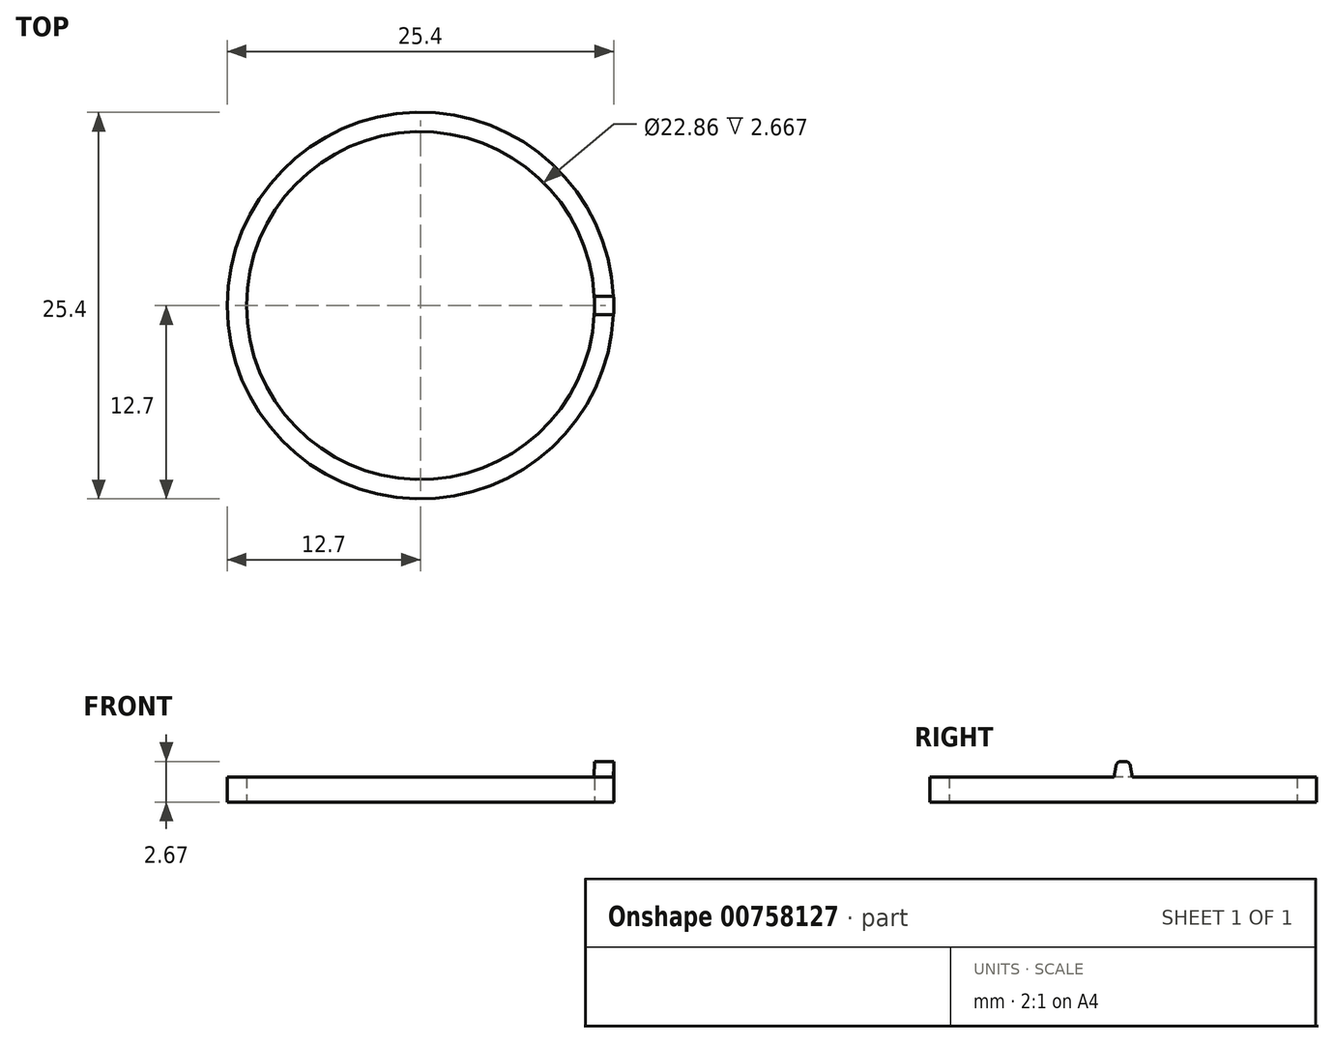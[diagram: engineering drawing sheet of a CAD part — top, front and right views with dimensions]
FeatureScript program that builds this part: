
annotation { "Feature Type Name" : "Feature", "Feature Type Description" : "" }
export const myFeature = defineFeature(function(context is Context, id is Id, definition is map)
    precondition{}
    {
        {
            var Q0;
            Q0=qCreatedBy(makeId("Top.planeOp"),FACE);
            var sketch = newSketch(context, id + "F0", { "sketchPlane" : qUnion([Q0])});
            skCircle(sketch, "E0", {"center": v(0, 0) * mm, "radius": 9.52 * mm});
            skCircle(sketch, "E1", {"center": v(0, 0) * mm, "radius": 12.7 * mm});
            skSolve(sketch);
        }
        {
            var Q0;
            Q0 = qSketchRegion(id + "F0", true);
            extrude(context, id + "F1", {"entities" : qUnion([Q0]), "depth" : 9.27 * mm, "offsetDistance" : 25.4 * mm});
        }
        {
            var Q0;
            Q0=makeQuery(id+"F1.opExtrude","CAP_FACE",FACE,{"disambiguationData":[OSD([sQuery(id+"F0.wireOp",EDGE,"E0"),sQuery(id+"F0.wireOp",EDGE,"E1")])],"isStart":false});
            var sketch = newSketch(context, id + "F2", { "sketchPlane" : qUnion([Q0])});
            skCircle(sketch, "E2", {"center": v(0, 0) * mm, "radius": 19.05 * mm});
            skCircle(sketch, "E3", {"center": v(0, 0) * mm, "radius": 10.8 * mm});
            skSolve(sketch);
        }
        {
            var Q0;
            Q0=makeQuery(id+"F2.imprint","IMPRINT",FACE,{"disambiguationData":[TD([[makeQuery(id+"F2.imprint","IMPRINT",EDGE,{"derivedFrom":sQuery(id+"F2.wireOp",EDGE,"E3")}),-1.0]])]});
            extrude(context, id + "F3", {"entities" : qUnion([Q0]), "operationType" : NewBodyOperationType.REMOVE, "oppositeDirection" : true, "depth" : 7.62 * mm, "offsetDistance" : 25.4 * mm});
        }
        {
            var Q0;
            Q0=qCreatedBy(makeId("Right.planeOp"),FACE);
            cPlane(context, id + "F4", {"entities" : qUnion([Q0]), "cplaneType" : CPlaneType.OFFSET, "offset" : 10.16 * mm, "width" : 152.4 * mm, "height" : 152.4 * mm});
        }
        {
            var Q0;
            Q0=qCreatedBy(id+"F4.planeOp",FACE);
            var sketch = newSketch(context, id + "F5", { "sketchPlane" : qUnion([Q0])});
            skLineSegment(sketch, "E4", {"start": v(-0.6, 1.65) * mm, "end": v(-0.42, 2.67) * mm});
            skLineSegment(sketch, "E5", {"start": v(-0.42, 2.67) * mm, "end": v(0.42, 2.67) * mm});
            skLineSegment(sketch, "E6", {"start": v(0.42, 2.67) * mm, "end": v(0.6, 1.65) * mm});
            skLineSegment(sketch, "E7", {"start": v(-0.6, 1.65) * mm, "end": v(0.6, 1.65) * mm});
            skSolve(sketch);
        }
        {
            var Q0;
            Q0 = qSketchRegion(id + "F5", true);
            var Q1;
            Q1=makeQuery(id+"F1.opExtrude","SWEPT_FACE",FACE,{"disambiguationData":[OSD([sQuery(id+"F0.wireOp",EDGE,"E1")])]});
            extrude(context, id + "F6", {"entities" : qUnion([Q0]), "operationType" : NewBodyOperationType.ADD, "endBound" : BoundingType.UP_TO_SURFACE, "depth" : 25.4 * mm, "endBoundEntityFace" : qUnion([Q1]), "offsetDistance" : 25.4 * mm});
        }
        {
            var Q0;
            Q0=qCreatedBy(makeId("Front.planeOp"),FACE);
            var sketch = newSketch(context, id + "F7", { "sketchPlane" : qUnion([Q0])});
            skLineSegment(sketch, "E8", {"start": v(0, 28.15) * mm, "end": v(0, -16.82) * mm});
            skSolve(sketch);
        }
        {
            var Q0;
            Q0=makeQuery(id+"FndBxbkuIEqvg3Y_1.3.F6.opExtrude","SWEPT_EDGE",EDGE,{"disambiguationData":[OSD([sQuery(id+"F5.wireOp",EDGE,"E6"),sQuery(id+"F5.wireOp",EDGE,"E7")])]});
            var Q1;
            Q1=makeQuery(id+"FndBxbkuIEqvg3Y_1.3.F6.opExtrude","SWEPT_EDGE",EDGE,{"disambiguationData":[OSD([sQuery(id+"F5.wireOp",EDGE,"E5"),sQuery(id+"F5.wireOp",EDGE,"E6")])]});
            var Q2;
            Q2=makeQuery(id+"FndBxbkuIEqvg3Y_1.3.F6.opExtrude","SWEPT_EDGE",EDGE,{"disambiguationData":[OSD([sQuery(id+"F5.wireOp",EDGE,"E4"),sQuery(id+"F5.wireOp",EDGE,"E5")])]});
            var Q3;
            Q3=makeQuery(id+"FndBxbkuIEqvg3Y_1.3.F6.opExtrude","SWEPT_EDGE",EDGE,{"disambiguationData":[OSD([sQuery(id+"F5.wireOp",EDGE,"E4"),sQuery(id+"F5.wireOp",EDGE,"E7")])]});
            var Q4;
            Q4=makeQuery(id+"FndBxbkuIEqvg3Y_1.2.F6.opExtrude","SWEPT_EDGE",EDGE,{"disambiguationData":[OSD([sQuery(id+"F5.wireOp",EDGE,"E4"),sQuery(id+"F5.wireOp",EDGE,"E7")])]});
            var Q5;
            Q5=makeQuery(id+"FndBxbkuIEqvg3Y_1.2.F6.opExtrude","SWEPT_EDGE",EDGE,{"disambiguationData":[OSD([sQuery(id+"F5.wireOp",EDGE,"E4"),sQuery(id+"F5.wireOp",EDGE,"E5")])]});
            var Q6;
            Q6=makeQuery(id+"FndBxbkuIEqvg3Y_1.2.F6.opExtrude","SWEPT_EDGE",EDGE,{"disambiguationData":[OSD([sQuery(id+"F5.wireOp",EDGE,"E5"),sQuery(id+"F5.wireOp",EDGE,"E6")])]});
            var Q7;
            Q7=makeQuery(id+"FndBxbkuIEqvg3Y_1.2.F6.opExtrude","SWEPT_EDGE",EDGE,{"disambiguationData":[OSD([sQuery(id+"F5.wireOp",EDGE,"E6"),sQuery(id+"F5.wireOp",EDGE,"E7")])]});
            var Q8;
            Q8=makeQuery(id+"FndBxbkuIEqvg3Y_1.1.F6.opExtrude","SWEPT_EDGE",EDGE,{"disambiguationData":[OSD([sQuery(id+"F5.wireOp",EDGE,"E4"),sQuery(id+"F5.wireOp",EDGE,"E7")])]});
            var Q9;
            Q9=makeQuery(id+"FndBxbkuIEqvg3Y_1.1.F6.opExtrude","SWEPT_EDGE",EDGE,{"disambiguationData":[OSD([sQuery(id+"F5.wireOp",EDGE,"E4"),sQuery(id+"F5.wireOp",EDGE,"E5")])]});
            var Q10;
            Q10=makeQuery(id+"FndBxbkuIEqvg3Y_1.1.F6.opExtrude","SWEPT_EDGE",EDGE,{"disambiguationData":[OSD([sQuery(id+"F5.wireOp",EDGE,"E5"),sQuery(id+"F5.wireOp",EDGE,"E6")])]});
            var Q11;
            Q11=makeQuery(id+"FndBxbkuIEqvg3Y_1.1.F6.opExtrude","SWEPT_EDGE",EDGE,{"disambiguationData":[OSD([sQuery(id+"F5.wireOp",EDGE,"E6"),sQuery(id+"F5.wireOp",EDGE,"E7")])]});
            var Q12;
            Q12=makeQuery(id+"F6.opExtrude","SWEPT_EDGE",EDGE,{"disambiguationData":[OSD([sQuery(id+"F5.wireOp",EDGE,"E4"),sQuery(id+"F5.wireOp",EDGE,"E7")])]});
            var Q13;
            Q13=makeQuery(id+"F6.opExtrude","SWEPT_EDGE",EDGE,{"disambiguationData":[OSD([sQuery(id+"F5.wireOp",EDGE,"E4"),sQuery(id+"F5.wireOp",EDGE,"E5")])]});
            var Q14;
            Q14=makeQuery(id+"F6.opExtrude","SWEPT_EDGE",EDGE,{"disambiguationData":[OSD([sQuery(id+"F5.wireOp",EDGE,"E5"),sQuery(id+"F5.wireOp",EDGE,"E6")])]});
            var Q15;
            Q15=makeQuery(id+"F6.opExtrude","SWEPT_EDGE",EDGE,{"disambiguationData":[OSD([sQuery(id+"F5.wireOp",EDGE,"E6"),sQuery(id+"F5.wireOp",EDGE,"E7")])]});
            var Q16;
            Q16=makeQuery(id+"FndBxbkuIEqvg3Y_1.31.F6.opExtrude","SWEPT_EDGE",EDGE,{"disambiguationData":[OSD([sQuery(id+"F5.wireOp",EDGE,"E4"),sQuery(id+"F5.wireOp",EDGE,"E7")])]});
            var Q17;
            Q17=makeQuery(id+"FndBxbkuIEqvg3Y_1.31.F6.opExtrude","SWEPT_EDGE",EDGE,{"disambiguationData":[OSD([sQuery(id+"F5.wireOp",EDGE,"E4"),sQuery(id+"F5.wireOp",EDGE,"E5")])]});
            var Q18;
            Q18=makeQuery(id+"FndBxbkuIEqvg3Y_1.31.F6.opExtrude","SWEPT_EDGE",EDGE,{"disambiguationData":[OSD([sQuery(id+"F5.wireOp",EDGE,"E5"),sQuery(id+"F5.wireOp",EDGE,"E6")])]});
            var Q19;
            Q19=makeQuery(id+"FndBxbkuIEqvg3Y_1.31.F6.opExtrude","SWEPT_EDGE",EDGE,{"disambiguationData":[OSD([sQuery(id+"F5.wireOp",EDGE,"E6"),sQuery(id+"F5.wireOp",EDGE,"E7")])]});
            var Q20;
            Q20=makeQuery(id+"FndBxbkuIEqvg3Y_1.30.F6.opExtrude","SWEPT_EDGE",EDGE,{"disambiguationData":[OSD([sQuery(id+"F5.wireOp",EDGE,"E4"),sQuery(id+"F5.wireOp",EDGE,"E7")])]});
            var Q21;
            Q21=makeQuery(id+"FndBxbkuIEqvg3Y_1.30.F6.opExtrude","SWEPT_EDGE",EDGE,{"disambiguationData":[OSD([sQuery(id+"F5.wireOp",EDGE,"E4"),sQuery(id+"F5.wireOp",EDGE,"E5")])]});
            var Q22;
            Q22=makeQuery(id+"FndBxbkuIEqvg3Y_1.30.F6.opExtrude","SWEPT_EDGE",EDGE,{"disambiguationData":[OSD([sQuery(id+"F5.wireOp",EDGE,"E5"),sQuery(id+"F5.wireOp",EDGE,"E6")])]});
            var Q23;
            Q23=makeQuery(id+"FndBxbkuIEqvg3Y_1.30.F6.opExtrude","SWEPT_EDGE",EDGE,{"disambiguationData":[OSD([sQuery(id+"F5.wireOp",EDGE,"E6"),sQuery(id+"F5.wireOp",EDGE,"E7")])]});
            var Q24;
            Q24=makeQuery(id+"FndBxbkuIEqvg3Y_1.29.F6.opExtrude","SWEPT_EDGE",EDGE,{"disambiguationData":[OSD([sQuery(id+"F5.wireOp",EDGE,"E4"),sQuery(id+"F5.wireOp",EDGE,"E7")])]});
            var Q25;
            Q25=makeQuery(id+"FndBxbkuIEqvg3Y_1.29.F6.opExtrude","SWEPT_EDGE",EDGE,{"disambiguationData":[OSD([sQuery(id+"F5.wireOp",EDGE,"E4"),sQuery(id+"F5.wireOp",EDGE,"E5")])]});
            var Q26;
            Q26=makeQuery(id+"FndBxbkuIEqvg3Y_1.29.F6.opExtrude","SWEPT_EDGE",EDGE,{"disambiguationData":[OSD([sQuery(id+"F5.wireOp",EDGE,"E5"),sQuery(id+"F5.wireOp",EDGE,"E6")])]});
            var Q27;
            Q27=makeQuery(id+"FndBxbkuIEqvg3Y_1.29.F6.opExtrude","SWEPT_EDGE",EDGE,{"disambiguationData":[OSD([sQuery(id+"F5.wireOp",EDGE,"E6"),sQuery(id+"F5.wireOp",EDGE,"E7")])]});
            var Q28;
            Q28=makeQuery(id+"FndBxbkuIEqvg3Y_1.28.F6.opExtrude","SWEPT_EDGE",EDGE,{"disambiguationData":[OSD([sQuery(id+"F5.wireOp",EDGE,"E4"),sQuery(id+"F5.wireOp",EDGE,"E5")])]});
            var Q29;
            Q29=makeQuery(id+"FndBxbkuIEqvg3Y_1.28.F6.opExtrude","SWEPT_EDGE",EDGE,{"disambiguationData":[OSD([sQuery(id+"F5.wireOp",EDGE,"E4"),sQuery(id+"F5.wireOp",EDGE,"E7")])]});
            var Q30;
            Q30=makeQuery(id+"FndBxbkuIEqvg3Y_1.28.F6.opExtrude","SWEPT_EDGE",EDGE,{"disambiguationData":[OSD([sQuery(id+"F5.wireOp",EDGE,"E5"),sQuery(id+"F5.wireOp",EDGE,"E6")])]});
            var Q31;
            Q31=makeQuery(id+"FndBxbkuIEqvg3Y_1.28.F6.opExtrude","SWEPT_EDGE",EDGE,{"disambiguationData":[OSD([sQuery(id+"F5.wireOp",EDGE,"E6"),sQuery(id+"F5.wireOp",EDGE,"E7")])]});
            var Q32;
            Q32=makeQuery(id+"FndBxbkuIEqvg3Y_1.27.F6.opExtrude","SWEPT_EDGE",EDGE,{"disambiguationData":[OSD([sQuery(id+"F5.wireOp",EDGE,"E4"),sQuery(id+"F5.wireOp",EDGE,"E7")])]});
            var Q33;
            Q33=makeQuery(id+"FndBxbkuIEqvg3Y_1.27.F6.opExtrude","SWEPT_EDGE",EDGE,{"disambiguationData":[OSD([sQuery(id+"F5.wireOp",EDGE,"E4"),sQuery(id+"F5.wireOp",EDGE,"E5")])]});
            var Q34;
            Q34=makeQuery(id+"FndBxbkuIEqvg3Y_1.27.F6.opExtrude","SWEPT_EDGE",EDGE,{"disambiguationData":[OSD([sQuery(id+"F5.wireOp",EDGE,"E5"),sQuery(id+"F5.wireOp",EDGE,"E6")])]});
            var Q35;
            Q35=makeQuery(id+"FndBxbkuIEqvg3Y_1.26.F6.opExtrude","SWEPT_EDGE",EDGE,{"disambiguationData":[OSD([sQuery(id+"F5.wireOp",EDGE,"E4"),sQuery(id+"F5.wireOp",EDGE,"E7")])]});
            var Q36;
            Q36=makeQuery(id+"FndBxbkuIEqvg3Y_1.26.F6.opExtrude","SWEPT_EDGE",EDGE,{"disambiguationData":[OSD([sQuery(id+"F5.wireOp",EDGE,"E4"),sQuery(id+"F5.wireOp",EDGE,"E5")])]});
            var Q37;
            Q37=makeQuery(id+"FndBxbkuIEqvg3Y_1.26.F6.opExtrude","SWEPT_EDGE",EDGE,{"disambiguationData":[OSD([sQuery(id+"F5.wireOp",EDGE,"E5"),sQuery(id+"F5.wireOp",EDGE,"E6")])]});
            var Q38;
            Q38=makeQuery(id+"FndBxbkuIEqvg3Y_1.25.F6.opExtrude","SWEPT_EDGE",EDGE,{"disambiguationData":[OSD([sQuery(id+"F5.wireOp",EDGE,"E4"),sQuery(id+"F5.wireOp",EDGE,"E7")])]});
            var Q39;
            Q39=makeQuery(id+"FndBxbkuIEqvg3Y_1.25.F6.opExtrude","SWEPT_EDGE",EDGE,{"disambiguationData":[OSD([sQuery(id+"F5.wireOp",EDGE,"E4"),sQuery(id+"F5.wireOp",EDGE,"E5")])]});
            var Q40;
            Q40=makeQuery(id+"FndBxbkuIEqvg3Y_1.25.F6.opExtrude","SWEPT_EDGE",EDGE,{"disambiguationData":[OSD([sQuery(id+"F5.wireOp",EDGE,"E5"),sQuery(id+"F5.wireOp",EDGE,"E6")])]});
            var Q41;
            Q41=makeQuery(id+"FndBxbkuIEqvg3Y_1.27.F6.opExtrude","SWEPT_EDGE",EDGE,{"disambiguationData":[OSD([sQuery(id+"F5.wireOp",EDGE,"E6"),sQuery(id+"F5.wireOp",EDGE,"E7")])]});
            var Q42;
            Q42=makeQuery(id+"FndBxbkuIEqvg3Y_1.26.F6.opExtrude","SWEPT_EDGE",EDGE,{"disambiguationData":[OSD([sQuery(id+"F5.wireOp",EDGE,"E6"),sQuery(id+"F5.wireOp",EDGE,"E7")])]});
            var Q43;
            Q43=makeQuery(id+"FndBxbkuIEqvg3Y_1.25.F6.opExtrude","SWEPT_EDGE",EDGE,{"disambiguationData":[OSD([sQuery(id+"F5.wireOp",EDGE,"E6"),sQuery(id+"F5.wireOp",EDGE,"E7")])]});
            var Q44;
            Q44=makeQuery(id+"FndBxbkuIEqvg3Y_1.4.F6.opExtrude","SWEPT_EDGE",EDGE,{"disambiguationData":[OSD([sQuery(id+"F5.wireOp",EDGE,"E6"),sQuery(id+"F5.wireOp",EDGE,"E7")])]});
            var Q45;
            Q45=makeQuery(id+"FndBxbkuIEqvg3Y_1.4.F6.opExtrude","SWEPT_EDGE",EDGE,{"disambiguationData":[OSD([sQuery(id+"F5.wireOp",EDGE,"E5"),sQuery(id+"F5.wireOp",EDGE,"E6")])]});
            var Q46;
            Q46=makeQuery(id+"FndBxbkuIEqvg3Y_1.6.F6.opExtrude","SWEPT_EDGE",EDGE,{"disambiguationData":[OSD([sQuery(id+"F5.wireOp",EDGE,"E5"),sQuery(id+"F5.wireOp",EDGE,"E6")])]});
            var Q47;
            Q47=makeQuery(id+"FndBxbkuIEqvg3Y_1.6.F6.opExtrude","SWEPT_EDGE",EDGE,{"disambiguationData":[OSD([sQuery(id+"F5.wireOp",EDGE,"E6"),sQuery(id+"F5.wireOp",EDGE,"E7")])]});
            var Q48;
            Q48=makeQuery(id+"FndBxbkuIEqvg3Y_1.5.F6.opExtrude","SWEPT_EDGE",EDGE,{"disambiguationData":[OSD([sQuery(id+"F5.wireOp",EDGE,"E5"),sQuery(id+"F5.wireOp",EDGE,"E6")])]});
            var Q49;
            Q49=makeQuery(id+"FndBxbkuIEqvg3Y_1.5.F6.opExtrude","SWEPT_EDGE",EDGE,{"disambiguationData":[OSD([sQuery(id+"F5.wireOp",EDGE,"E6"),sQuery(id+"F5.wireOp",EDGE,"E7")])]});
            var Q50;
            Q50=makeQuery(id+"FndBxbkuIEqvg3Y_1.8.F6.opExtrude","SWEPT_EDGE",EDGE,{"disambiguationData":[OSD([sQuery(id+"F5.wireOp",EDGE,"E5"),sQuery(id+"F5.wireOp",EDGE,"E6")])]});
            var Q51;
            Q51=makeQuery(id+"FndBxbkuIEqvg3Y_1.7.F6.opExtrude","SWEPT_EDGE",EDGE,{"disambiguationData":[OSD([sQuery(id+"F5.wireOp",EDGE,"E5"),sQuery(id+"F5.wireOp",EDGE,"E6")])]});
            var Q52;
            Q52=makeQuery(id+"FndBxbkuIEqvg3Y_1.8.F6.opExtrude","SWEPT_EDGE",EDGE,{"disambiguationData":[OSD([sQuery(id+"F5.wireOp",EDGE,"E6"),sQuery(id+"F5.wireOp",EDGE,"E7")])]});
            var Q53;
            Q53=makeQuery(id+"FndBxbkuIEqvg3Y_1.7.F6.opExtrude","SWEPT_EDGE",EDGE,{"disambiguationData":[OSD([sQuery(id+"F5.wireOp",EDGE,"E6"),sQuery(id+"F5.wireOp",EDGE,"E7")])]});
            var Q54;
            Q54=makeQuery(id+"FndBxbkuIEqvg3Y_1.4.F6.opExtrude","SWEPT_EDGE",EDGE,{"disambiguationData":[OSD([sQuery(id+"F5.wireOp",EDGE,"E4"),sQuery(id+"F5.wireOp",EDGE,"E5")])]});
            var Q55;
            Q55=makeQuery(id+"FndBxbkuIEqvg3Y_1.4.F6.opExtrude","SWEPT_EDGE",EDGE,{"disambiguationData":[OSD([sQuery(id+"F5.wireOp",EDGE,"E4"),sQuery(id+"F5.wireOp",EDGE,"E7")])]});
            var Q56;
            Q56=makeQuery(id+"FndBxbkuIEqvg3Y_1.5.F6.opExtrude","SWEPT_EDGE",EDGE,{"disambiguationData":[OSD([sQuery(id+"F5.wireOp",EDGE,"E4"),sQuery(id+"F5.wireOp",EDGE,"E5")])]});
            var Q57;
            Q57=makeQuery(id+"FndBxbkuIEqvg3Y_1.5.F6.opExtrude","SWEPT_EDGE",EDGE,{"disambiguationData":[OSD([sQuery(id+"F5.wireOp",EDGE,"E4"),sQuery(id+"F5.wireOp",EDGE,"E7")])]});
            var Q58;
            Q58=makeQuery(id+"FndBxbkuIEqvg3Y_1.6.F6.opExtrude","SWEPT_EDGE",EDGE,{"disambiguationData":[OSD([sQuery(id+"F5.wireOp",EDGE,"E4"),sQuery(id+"F5.wireOp",EDGE,"E5")])]});
            var Q59;
            Q59=makeQuery(id+"FndBxbkuIEqvg3Y_1.6.F6.opExtrude","SWEPT_EDGE",EDGE,{"disambiguationData":[OSD([sQuery(id+"F5.wireOp",EDGE,"E4"),sQuery(id+"F5.wireOp",EDGE,"E7")])]});
            var Q60;
            Q60=makeQuery(id+"FndBxbkuIEqvg3Y_1.7.F6.opExtrude","SWEPT_EDGE",EDGE,{"disambiguationData":[OSD([sQuery(id+"F5.wireOp",EDGE,"E4"),sQuery(id+"F5.wireOp",EDGE,"E5")])]});
            var Q61;
            Q61=makeQuery(id+"FndBxbkuIEqvg3Y_1.7.F6.opExtrude","SWEPT_EDGE",EDGE,{"disambiguationData":[OSD([sQuery(id+"F5.wireOp",EDGE,"E4"),sQuery(id+"F5.wireOp",EDGE,"E7")])]});
            var Q62;
            Q62=makeQuery(id+"FndBxbkuIEqvg3Y_1.8.F6.opExtrude","SWEPT_EDGE",EDGE,{"disambiguationData":[OSD([sQuery(id+"F5.wireOp",EDGE,"E4"),sQuery(id+"F5.wireOp",EDGE,"E7")])]});
            var Q63;
            Q63=makeQuery(id+"FndBxbkuIEqvg3Y_1.8.F6.opExtrude","SWEPT_EDGE",EDGE,{"disambiguationData":[OSD([sQuery(id+"F5.wireOp",EDGE,"E4"),sQuery(id+"F5.wireOp",EDGE,"E5")])]});
            var Q64;
            Q64=makeQuery(id+"FndBxbkuIEqvg3Y_1.9.F6.opExtrude","SWEPT_EDGE",EDGE,{"disambiguationData":[OSD([sQuery(id+"F5.wireOp",EDGE,"E6"),sQuery(id+"F5.wireOp",EDGE,"E7")])]});
            var Q65;
            Q65=makeQuery(id+"FndBxbkuIEqvg3Y_1.10.F6.opExtrude","SWEPT_EDGE",EDGE,{"disambiguationData":[OSD([sQuery(id+"F5.wireOp",EDGE,"E6"),sQuery(id+"F5.wireOp",EDGE,"E7")])]});
            var Q66;
            Q66=makeQuery(id+"FndBxbkuIEqvg3Y_1.11.F6.opExtrude","SWEPT_EDGE",EDGE,{"disambiguationData":[OSD([sQuery(id+"F5.wireOp",EDGE,"E6"),sQuery(id+"F5.wireOp",EDGE,"E7")])]});
            var Q67;
            Q67=makeQuery(id+"FndBxbkuIEqvg3Y_1.12.F6.opExtrude","SWEPT_EDGE",EDGE,{"disambiguationData":[OSD([sQuery(id+"F5.wireOp",EDGE,"E6"),sQuery(id+"F5.wireOp",EDGE,"E7")])]});
            var Q68;
            Q68=makeQuery(id+"FndBxbkuIEqvg3Y_1.11.F6.opExtrude","SWEPT_EDGE",EDGE,{"disambiguationData":[OSD([sQuery(id+"F5.wireOp",EDGE,"E5"),sQuery(id+"F5.wireOp",EDGE,"E6")])]});
            var Q69;
            Q69=makeQuery(id+"FndBxbkuIEqvg3Y_1.10.F6.opExtrude","SWEPT_EDGE",EDGE,{"disambiguationData":[OSD([sQuery(id+"F5.wireOp",EDGE,"E5"),sQuery(id+"F5.wireOp",EDGE,"E6")])]});
            var Q70;
            Q70=makeQuery(id+"FndBxbkuIEqvg3Y_1.9.F6.opExtrude","SWEPT_EDGE",EDGE,{"disambiguationData":[OSD([sQuery(id+"F5.wireOp",EDGE,"E5"),sQuery(id+"F5.wireOp",EDGE,"E6")])]});
            var Q71;
            Q71=makeQuery(id+"FndBxbkuIEqvg3Y_1.11.F6.opExtrude","SWEPT_EDGE",EDGE,{"disambiguationData":[OSD([sQuery(id+"F5.wireOp",EDGE,"E4"),sQuery(id+"F5.wireOp",EDGE,"E5")])]});
            var Q72;
            Q72=makeQuery(id+"FndBxbkuIEqvg3Y_1.10.F6.opExtrude","SWEPT_EDGE",EDGE,{"disambiguationData":[OSD([sQuery(id+"F5.wireOp",EDGE,"E4"),sQuery(id+"F5.wireOp",EDGE,"E5")])]});
            var Q73;
            Q73=makeQuery(id+"FndBxbkuIEqvg3Y_1.11.F6.opExtrude","SWEPT_EDGE",EDGE,{"disambiguationData":[OSD([sQuery(id+"F5.wireOp",EDGE,"E4"),sQuery(id+"F5.wireOp",EDGE,"E7")])]});
            var Q74;
            Q74=makeQuery(id+"FndBxbkuIEqvg3Y_1.10.F6.opExtrude","SWEPT_EDGE",EDGE,{"disambiguationData":[OSD([sQuery(id+"F5.wireOp",EDGE,"E4"),sQuery(id+"F5.wireOp",EDGE,"E7")])]});
            var Q75;
            Q75=makeQuery(id+"FndBxbkuIEqvg3Y_1.9.F6.opExtrude","SWEPT_EDGE",EDGE,{"disambiguationData":[OSD([sQuery(id+"F5.wireOp",EDGE,"E4"),sQuery(id+"F5.wireOp",EDGE,"E5")])]});
            var Q76;
            Q76=makeQuery(id+"FndBxbkuIEqvg3Y_1.9.F6.opExtrude","SWEPT_EDGE",EDGE,{"disambiguationData":[OSD([sQuery(id+"F5.wireOp",EDGE,"E4"),sQuery(id+"F5.wireOp",EDGE,"E7")])]});
            var Q77;
            Q77=makeQuery(id+"FndBxbkuIEqvg3Y_1.12.F6.opExtrude","SWEPT_EDGE",EDGE,{"disambiguationData":[OSD([sQuery(id+"F5.wireOp",EDGE,"E5"),sQuery(id+"F5.wireOp",EDGE,"E6")])]});
            var Q78;
            Q78=makeQuery(id+"FndBxbkuIEqvg3Y_1.12.F6.opExtrude","SWEPT_EDGE",EDGE,{"disambiguationData":[OSD([sQuery(id+"F5.wireOp",EDGE,"E4"),sQuery(id+"F5.wireOp",EDGE,"E5")])]});
            var Q79;
            Q79=makeQuery(id+"FndBxbkuIEqvg3Y_1.13.F6.opExtrude","SWEPT_EDGE",EDGE,{"disambiguationData":[OSD([sQuery(id+"F5.wireOp",EDGE,"E6"),sQuery(id+"F5.wireOp",EDGE,"E7")])]});
            var Q80;
            Q80=makeQuery(id+"FndBxbkuIEqvg3Y_1.13.F6.opExtrude","SWEPT_EDGE",EDGE,{"disambiguationData":[OSD([sQuery(id+"F5.wireOp",EDGE,"E5"),sQuery(id+"F5.wireOp",EDGE,"E6")])]});
            var Q81;
            Q81=makeQuery(id+"FndBxbkuIEqvg3Y_1.13.F6.opExtrude","SWEPT_EDGE",EDGE,{"disambiguationData":[OSD([sQuery(id+"F5.wireOp",EDGE,"E4"),sQuery(id+"F5.wireOp",EDGE,"E5")])]});
            var Q82;
            Q82=makeQuery(id+"FndBxbkuIEqvg3Y_1.14.F6.opExtrude","SWEPT_EDGE",EDGE,{"disambiguationData":[OSD([sQuery(id+"F5.wireOp",EDGE,"E6"),sQuery(id+"F5.wireOp",EDGE,"E7")])]});
            var Q83;
            Q83=makeQuery(id+"FndBxbkuIEqvg3Y_1.14.F6.opExtrude","SWEPT_EDGE",EDGE,{"disambiguationData":[OSD([sQuery(id+"F5.wireOp",EDGE,"E5"),sQuery(id+"F5.wireOp",EDGE,"E6")])]});
            var Q84;
            Q84=makeQuery(id+"FndBxbkuIEqvg3Y_1.14.F6.opExtrude","SWEPT_EDGE",EDGE,{"disambiguationData":[OSD([sQuery(id+"F5.wireOp",EDGE,"E4"),sQuery(id+"F5.wireOp",EDGE,"E5")])]});
            var Q85;
            Q85=makeQuery(id+"FndBxbkuIEqvg3Y_1.15.F6.opExtrude","SWEPT_EDGE",EDGE,{"disambiguationData":[OSD([sQuery(id+"F5.wireOp",EDGE,"E6"),sQuery(id+"F5.wireOp",EDGE,"E7")])]});
            var Q86;
            Q86=makeQuery(id+"FndBxbkuIEqvg3Y_1.15.F6.opExtrude","SWEPT_EDGE",EDGE,{"disambiguationData":[OSD([sQuery(id+"F5.wireOp",EDGE,"E5"),sQuery(id+"F5.wireOp",EDGE,"E6")])]});
            var Q87;
            Q87=makeQuery(id+"FndBxbkuIEqvg3Y_1.15.F6.opExtrude","SWEPT_EDGE",EDGE,{"disambiguationData":[OSD([sQuery(id+"F5.wireOp",EDGE,"E4"),sQuery(id+"F5.wireOp",EDGE,"E5")])]});
            var Q88;
            Q88=makeQuery(id+"FndBxbkuIEqvg3Y_1.16.F6.opExtrude","SWEPT_EDGE",EDGE,{"disambiguationData":[OSD([sQuery(id+"F5.wireOp",EDGE,"E6"),sQuery(id+"F5.wireOp",EDGE,"E7")])]});
            var Q89;
            Q89=makeQuery(id+"FndBxbkuIEqvg3Y_1.16.F6.opExtrude","SWEPT_EDGE",EDGE,{"disambiguationData":[OSD([sQuery(id+"F5.wireOp",EDGE,"E5"),sQuery(id+"F5.wireOp",EDGE,"E6")])]});
            var Q90;
            Q90=makeQuery(id+"FndBxbkuIEqvg3Y_1.12.F6.opExtrude","SWEPT_EDGE",EDGE,{"disambiguationData":[OSD([sQuery(id+"F5.wireOp",EDGE,"E4"),sQuery(id+"F5.wireOp",EDGE,"E7")])]});
            var Q91;
            Q91=makeQuery(id+"FndBxbkuIEqvg3Y_1.13.F6.opExtrude","SWEPT_EDGE",EDGE,{"disambiguationData":[OSD([sQuery(id+"F5.wireOp",EDGE,"E4"),sQuery(id+"F5.wireOp",EDGE,"E7")])]});
            var Q92;
            Q92=makeQuery(id+"FndBxbkuIEqvg3Y_1.14.F6.opExtrude","SWEPT_EDGE",EDGE,{"disambiguationData":[OSD([sQuery(id+"F5.wireOp",EDGE,"E4"),sQuery(id+"F5.wireOp",EDGE,"E7")])]});
            var Q93;
            Q93=makeQuery(id+"FndBxbkuIEqvg3Y_1.15.F6.opExtrude","SWEPT_EDGE",EDGE,{"disambiguationData":[OSD([sQuery(id+"F5.wireOp",EDGE,"E4"),sQuery(id+"F5.wireOp",EDGE,"E7")])]});
            var Q94;
            Q94=makeQuery(id+"FndBxbkuIEqvg3Y_1.16.F6.opExtrude","SWEPT_EDGE",EDGE,{"disambiguationData":[OSD([sQuery(id+"F5.wireOp",EDGE,"E4"),sQuery(id+"F5.wireOp",EDGE,"E7")])]});
            var Q95;
            Q95=makeQuery(id+"FndBxbkuIEqvg3Y_1.16.F6.opExtrude","SWEPT_EDGE",EDGE,{"disambiguationData":[OSD([sQuery(id+"F5.wireOp",EDGE,"E4"),sQuery(id+"F5.wireOp",EDGE,"E5")])]});
            var Q96;
            Q96=makeQuery(id+"FndBxbkuIEqvg3Y_1.17.F6.opExtrude","SWEPT_EDGE",EDGE,{"disambiguationData":[OSD([sQuery(id+"F5.wireOp",EDGE,"E6"),sQuery(id+"F5.wireOp",EDGE,"E7")])]});
            var Q97;
            Q97=makeQuery(id+"FndBxbkuIEqvg3Y_1.17.F6.opExtrude","SWEPT_EDGE",EDGE,{"disambiguationData":[OSD([sQuery(id+"F5.wireOp",EDGE,"E5"),sQuery(id+"F5.wireOp",EDGE,"E6")])]});
            var Q98;
            Q98=makeQuery(id+"FndBxbkuIEqvg3Y_1.17.F6.opExtrude","SWEPT_EDGE",EDGE,{"disambiguationData":[OSD([sQuery(id+"F5.wireOp",EDGE,"E4"),sQuery(id+"F5.wireOp",EDGE,"E5")])]});
            var Q99;
            Q99=makeQuery(id+"FndBxbkuIEqvg3Y_1.17.F6.opExtrude","SWEPT_EDGE",EDGE,{"disambiguationData":[OSD([sQuery(id+"F5.wireOp",EDGE,"E4"),sQuery(id+"F5.wireOp",EDGE,"E7")])]});
            var Q100;
            Q100=makeQuery(id+"FndBxbkuIEqvg3Y_1.18.F6.opExtrude","SWEPT_EDGE",EDGE,{"disambiguationData":[OSD([sQuery(id+"F5.wireOp",EDGE,"E6"),sQuery(id+"F5.wireOp",EDGE,"E7")])]});
            var Q101;
            Q101=makeQuery(id+"FndBxbkuIEqvg3Y_1.18.F6.opExtrude","SWEPT_EDGE",EDGE,{"disambiguationData":[OSD([sQuery(id+"F5.wireOp",EDGE,"E5"),sQuery(id+"F5.wireOp",EDGE,"E6")])]});
            var Q102;
            Q102=makeQuery(id+"FndBxbkuIEqvg3Y_1.18.F6.opExtrude","SWEPT_EDGE",EDGE,{"disambiguationData":[OSD([sQuery(id+"F5.wireOp",EDGE,"E4"),sQuery(id+"F5.wireOp",EDGE,"E5")])]});
            var Q103;
            Q103=makeQuery(id+"FndBxbkuIEqvg3Y_1.19.F6.opExtrude","SWEPT_EDGE",EDGE,{"disambiguationData":[OSD([sQuery(id+"F5.wireOp",EDGE,"E6"),sQuery(id+"F5.wireOp",EDGE,"E7")])]});
            var Q104;
            Q104=makeQuery(id+"FndBxbkuIEqvg3Y_1.19.F6.opExtrude","SWEPT_EDGE",EDGE,{"disambiguationData":[OSD([sQuery(id+"F5.wireOp",EDGE,"E5"),sQuery(id+"F5.wireOp",EDGE,"E6")])]});
            var Q105;
            Q105=makeQuery(id+"FndBxbkuIEqvg3Y_1.20.F6.opExtrude","SWEPT_EDGE",EDGE,{"disambiguationData":[OSD([sQuery(id+"F5.wireOp",EDGE,"E6"),sQuery(id+"F5.wireOp",EDGE,"E7")])]});
            var Q106;
            Q106=makeQuery(id+"FndBxbkuIEqvg3Y_1.20.F6.opExtrude","SWEPT_EDGE",EDGE,{"disambiguationData":[OSD([sQuery(id+"F5.wireOp",EDGE,"E5"),sQuery(id+"F5.wireOp",EDGE,"E6")])]});
            var Q107;
            Q107=makeQuery(id+"FndBxbkuIEqvg3Y_1.21.F6.opExtrude","SWEPT_EDGE",EDGE,{"disambiguationData":[OSD([sQuery(id+"F5.wireOp",EDGE,"E6"),sQuery(id+"F5.wireOp",EDGE,"E7")])]});
            var Q108;
            Q108=makeQuery(id+"FndBxbkuIEqvg3Y_1.21.F6.opExtrude","SWEPT_EDGE",EDGE,{"disambiguationData":[OSD([sQuery(id+"F5.wireOp",EDGE,"E5"),sQuery(id+"F5.wireOp",EDGE,"E6")])]});
            var Q109;
            Q109=makeQuery(id+"FndBxbkuIEqvg3Y_1.21.F6.opExtrude","SWEPT_EDGE",EDGE,{"disambiguationData":[OSD([sQuery(id+"F5.wireOp",EDGE,"E4"),sQuery(id+"F5.wireOp",EDGE,"E5")])]});
            var Q110;
            Q110=makeQuery(id+"FndBxbkuIEqvg3Y_1.20.F6.opExtrude","SWEPT_EDGE",EDGE,{"disambiguationData":[OSD([sQuery(id+"F5.wireOp",EDGE,"E4"),sQuery(id+"F5.wireOp",EDGE,"E5")])]});
            var Q111;
            Q111=makeQuery(id+"FndBxbkuIEqvg3Y_1.18.F6.opExtrude","SWEPT_EDGE",EDGE,{"disambiguationData":[OSD([sQuery(id+"F5.wireOp",EDGE,"E4"),sQuery(id+"F5.wireOp",EDGE,"E7")])]});
            var Q112;
            Q112=makeQuery(id+"FndBxbkuIEqvg3Y_1.19.F6.opExtrude","SWEPT_EDGE",EDGE,{"disambiguationData":[OSD([sQuery(id+"F5.wireOp",EDGE,"E4"),sQuery(id+"F5.wireOp",EDGE,"E5")])]});
            var Q113;
            Q113=makeQuery(id+"FndBxbkuIEqvg3Y_1.19.F6.opExtrude","SWEPT_EDGE",EDGE,{"disambiguationData":[OSD([sQuery(id+"F5.wireOp",EDGE,"E4"),sQuery(id+"F5.wireOp",EDGE,"E7")])]});
            var Q114;
            Q114=makeQuery(id+"FndBxbkuIEqvg3Y_1.20.F6.opExtrude","SWEPT_EDGE",EDGE,{"disambiguationData":[OSD([sQuery(id+"F5.wireOp",EDGE,"E4"),sQuery(id+"F5.wireOp",EDGE,"E7")])]});
            var Q115;
            Q115=makeQuery(id+"FndBxbkuIEqvg3Y_1.21.F6.opExtrude","SWEPT_EDGE",EDGE,{"disambiguationData":[OSD([sQuery(id+"F5.wireOp",EDGE,"E4"),sQuery(id+"F5.wireOp",EDGE,"E7")])]});
            var Q116;
            Q116=makeQuery(id+"FndBxbkuIEqvg3Y_1.22.F6.opExtrude","SWEPT_EDGE",EDGE,{"disambiguationData":[OSD([sQuery(id+"F5.wireOp",EDGE,"E5"),sQuery(id+"F5.wireOp",EDGE,"E6")])]});
            var Q117;
            Q117=makeQuery(id+"FndBxbkuIEqvg3Y_1.22.F6.opExtrude","SWEPT_EDGE",EDGE,{"disambiguationData":[OSD([sQuery(id+"F5.wireOp",EDGE,"E4"),sQuery(id+"F5.wireOp",EDGE,"E5")])]});
            var Q118;
            Q118=makeQuery(id+"FndBxbkuIEqvg3Y_1.22.F6.opExtrude","SWEPT_EDGE",EDGE,{"disambiguationData":[OSD([sQuery(id+"F5.wireOp",EDGE,"E4"),sQuery(id+"F5.wireOp",EDGE,"E7")])]});
            var Q119;
            Q119=makeQuery(id+"FndBxbkuIEqvg3Y_1.23.F6.opExtrude","SWEPT_EDGE",EDGE,{"disambiguationData":[OSD([sQuery(id+"F5.wireOp",EDGE,"E6"),sQuery(id+"F5.wireOp",EDGE,"E7")])]});
            var Q120;
            Q120=makeQuery(id+"FndBxbkuIEqvg3Y_1.23.F6.opExtrude","SWEPT_EDGE",EDGE,{"disambiguationData":[OSD([sQuery(id+"F5.wireOp",EDGE,"E5"),sQuery(id+"F5.wireOp",EDGE,"E6")])]});
            var Q121;
            Q121=makeQuery(id+"FndBxbkuIEqvg3Y_1.23.F6.opExtrude","SWEPT_EDGE",EDGE,{"disambiguationData":[OSD([sQuery(id+"F5.wireOp",EDGE,"E4"),sQuery(id+"F5.wireOp",EDGE,"E5")])]});
            var Q122;
            Q122=makeQuery(id+"FndBxbkuIEqvg3Y_1.24.F6.opExtrude","SWEPT_EDGE",EDGE,{"disambiguationData":[OSD([sQuery(id+"F5.wireOp",EDGE,"E5"),sQuery(id+"F5.wireOp",EDGE,"E6")])]});
            var Q123;
            Q123=makeQuery(id+"FndBxbkuIEqvg3Y_1.24.F6.opExtrude","SWEPT_EDGE",EDGE,{"disambiguationData":[OSD([sQuery(id+"F5.wireOp",EDGE,"E4"),sQuery(id+"F5.wireOp",EDGE,"E5")])]});
            var Q124;
            Q124=makeQuery(id+"FndBxbkuIEqvg3Y_1.24.F6.opExtrude","SWEPT_EDGE",EDGE,{"disambiguationData":[OSD([sQuery(id+"F5.wireOp",EDGE,"E6"),sQuery(id+"F5.wireOp",EDGE,"E7")])]});
            var Q125;
            Q125=makeQuery(id+"FndBxbkuIEqvg3Y_1.22.F6.opExtrude","SWEPT_EDGE",EDGE,{"disambiguationData":[OSD([sQuery(id+"F5.wireOp",EDGE,"E6"),sQuery(id+"F5.wireOp",EDGE,"E7")])]});
            var Q126;
            Q126=makeQuery(id+"FndBxbkuIEqvg3Y_1.24.F6.opExtrude","SWEPT_EDGE",EDGE,{"disambiguationData":[OSD([sQuery(id+"F5.wireOp",EDGE,"E4"),sQuery(id+"F5.wireOp",EDGE,"E7")])]});
            var Q127;
            Q127=makeQuery(id+"FndBxbkuIEqvg3Y_1.23.F6.opExtrude","SWEPT_EDGE",EDGE,{"disambiguationData":[OSD([sQuery(id+"F5.wireOp",EDGE,"E4"),sQuery(id+"F5.wireOp",EDGE,"E7")])]});
            fillet(context, id + "F8", {"entities" : qUnion([Q0, Q1, Q2, Q3, Q4, Q5, Q6, Q7, Q8, Q9, Q10, Q11, Q12, Q13, Q14, Q15, Q16, Q17, Q18, Q19, Q20, Q21, Q22, Q23, Q24, Q25, Q26, Q27, Q28, Q29, Q30, Q31, Q32, Q33, Q34, Q35, Q36, Q37, Q38, Q39, Q40, Q41, Q42, Q43, Q44, Q45, Q46, Q47, Q48, Q49, Q50, Q51, Q52, Q53, Q54, Q55, Q56, Q57, Q58, Q59, Q60, Q61, Q62, Q63, Q64, Q65, Q66, Q67, Q68, Q69, Q70, Q71, Q72, Q73, Q74, Q75, Q76, Q77, Q78, Q79, Q80, Q81, Q82, Q83, Q84, Q85, Q86, Q87, Q88, Q89, Q90, Q91, Q92, Q93, Q94, Q95, Q96, Q97, Q98, Q99, Q100, Q101, Q102, Q103, Q104, Q105, Q106, Q107, Q108, Q109, Q110, Q111, Q112, Q113, Q114, Q115, Q116, Q117, Q118, Q119, Q120, Q121, Q122, Q123, Q124, Q125, Q126, Q127]), "radius" : 0.32 * mm, "tangentPropagation" : true, "allowEdgeOverflow" : false});
        }
        {
            var Q0;
            Q0=qCreatedBy(makeId("Right.planeOp"),FACE);
            var sketch = newSketch(context, id + "F9", { "sketchPlane" : qUnion([Q0])});
            skLineSegment(sketch, "E9.bottom", {"start": v(-12.7, 10.16) * mm, "end": v(12.7, 10.16) * mm});
            skLineSegment(sketch, "E9.top", {"start": v(-12.7, 3.17) * mm, "end": v(12.7, 3.17) * mm});
            skLineSegment(sketch, "E9.left", {"start": v(-12.7, 10.16) * mm, "end": v(-12.7, 3.17) * mm});
            skLineSegment(sketch, "E9.right", {"start": v(12.7, 10.16) * mm, "end": v(12.7, 3.17) * mm});
            skSolve(sketch);
        }
        {
            var Q0;
            Q0=makeQuery(id+"F9.imprint","IMPRINT",FACE,{"disambiguationData":[TD([[makeQuery(id+"F9.imprint","IMPRINT",EDGE,{"derivedFrom":sQuery(id+"F9.wireOp",EDGE,"E9.bottom")}),-1.0]])]});
            extrude(context, id + "F10", {"entities" : qUnion([Q0]), "operationType" : NewBodyOperationType.REMOVE, "endBound" : BoundingType.SYMMETRIC, "oppositeDirection" : true, "depth" : 38.1 * mm, "offsetDistance" : 25.4 * mm});
        }
        {
            var Q0;
            Q0=makeQuery(id+"F1.opExtrude","CAP_FACE",FACE,{"disambiguationData":[OSD([sQuery(id+"F0.wireOp",EDGE,"E0"),sQuery(id+"F0.wireOp",EDGE,"E1")])],"isStart":true});
            var sketch = newSketch(context, id + "F11", { "sketchPlane" : qUnion([Q0])});
            skCircle(sketch, "E10", {"center": v(0, 0) * mm, "radius": 11.43 * mm});
            skSolve(sketch);
        }
        {
            var Q0;
            Q0 = qSketchRegion(id + "F11", true);
            extrude(context, id + "F12", {"entities" : qUnion([Q0]), "operationType" : NewBodyOperationType.REMOVE, "endBound" : BoundingType.THROUGH_ALL, "oppositeDirection" : true, "depth" : 25.4 * mm, "offsetDistance" : 25.4 * mm});
        }
    });
